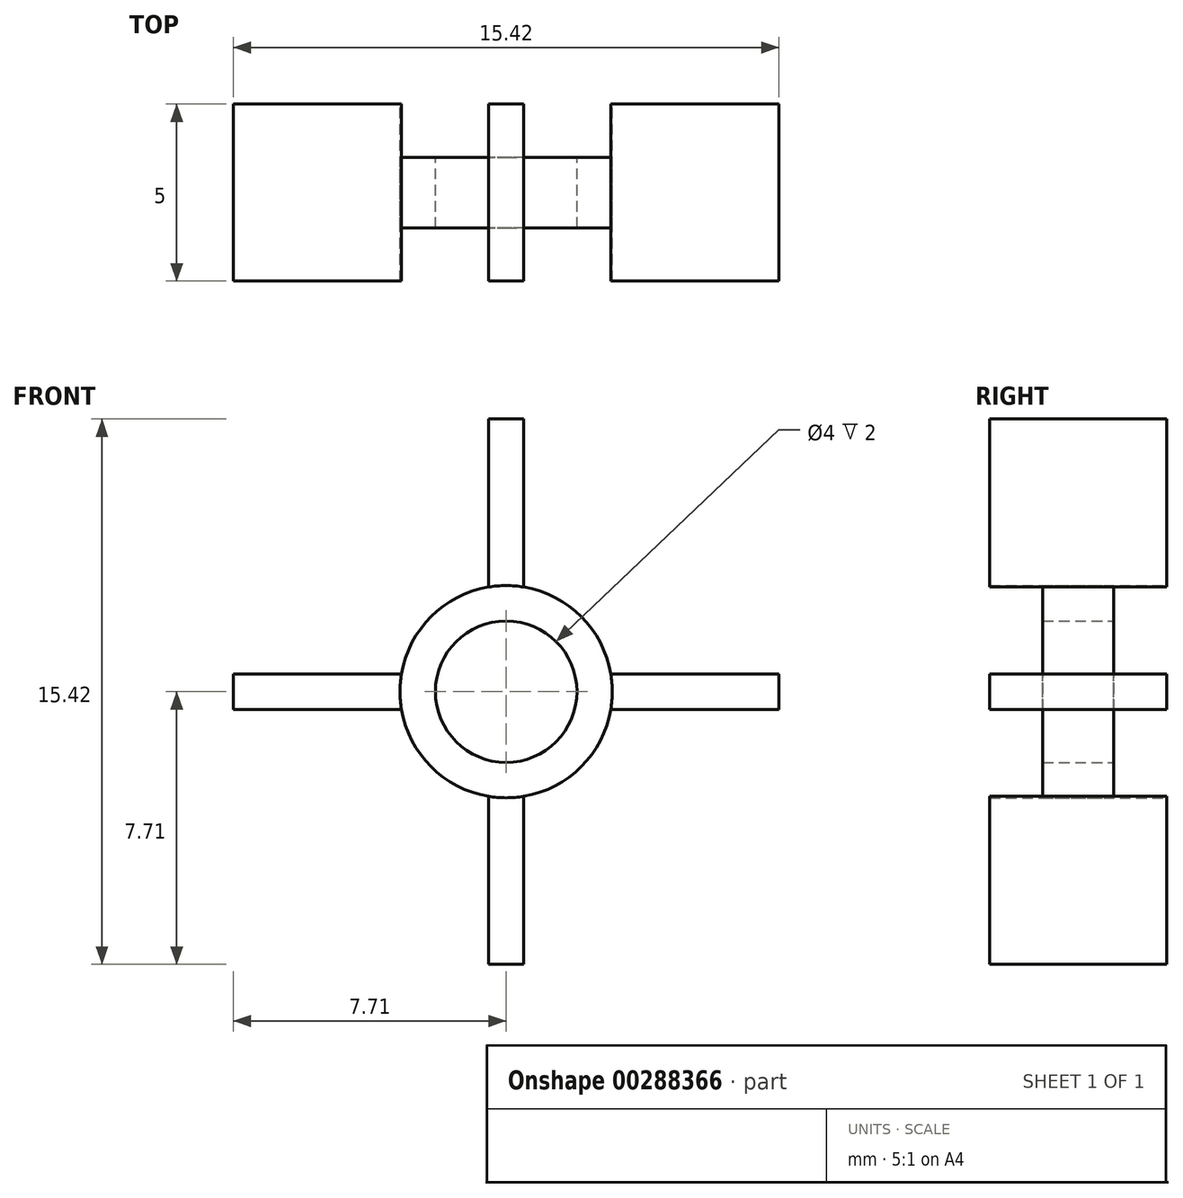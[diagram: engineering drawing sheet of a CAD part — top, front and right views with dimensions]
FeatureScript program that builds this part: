
annotation { "Feature Type Name" : "Feature", "Feature Type Description" : "" }
export const myFeature = defineFeature(function(context is Context, id is Id, definition is map)
    precondition{}
    {
        {
            var Q0;
            Q0=qCreatedBy(makeId("Front.planeOp"),FACE);
            var sketch = newSketch(context, id + "F0", { "sketchPlane" : qUnion([Q0])});
            skCircle(sketch, "E0", {"center": v(0, 0) * mm, "radius": 2 * mm});
            skCircle(sketch, "E1.0", {"center": v(0, 0) * mm, "radius": 3 * mm});
            skLineSegment(sketch, "E2.bottom", {"start": v(2.96, 0.5) * mm, "end": v(7.7, 0.5) * mm});
            skLineSegment(sketch, "E2.top", {"start": v(2.96, -0.5) * mm, "end": v(7.7, -0.5) * mm});
            skLineSegment(sketch, "E2.right", {"start": v(7.7, 0.5) * mm, "end": v(7.7, -0.5) * mm});
            skPoint(sketch, "E2.middle", {"position": v(5.33, 0) * mm});
            skLineSegment(sketch, "E3", {"start": v(0, 3) * mm, "end": v(0, -3) * mm, "construction": true});
            skPoint(sketch, "E4.MirrorP", {"position": v(-5.33, 0) * mm});
            skLineSegment(sketch, "E5.MirrorCS", {"start": v(-7.7, 0.5) * mm, "end": v(-7.7, -0.5) * mm});
            skLineSegment(sketch, "E6.MirrorCS", {"start": v(-2.96, 0.5) * mm, "end": v(-7.7, 0.5) * mm});
            skLineSegment(sketch, "E7.MirrorCS", {"start": v(-2.96, -0.5) * mm, "end": v(-7.7, -0.5) * mm});
            skLineSegment(sketch, "E8.top", {"start": v(0.5, 7.7) * mm, "end": v(-0.5, 7.7) * mm});
            skLineSegment(sketch, "E8.left", {"start": v(0.5, 2.96) * mm, "end": v(0.5, 7.7) * mm});
            skLineSegment(sketch, "E8.right", {"start": v(-0.5, 2.96) * mm, "end": v(-0.5, 7.7) * mm});
            skPoint(sketch, "E8.middle", {"position": v(0, 5.33) * mm});
            skLineSegment(sketch, "E9", {"start": v(-3, 0) * mm, "end": v(3, 0) * mm, "construction": true});
            skLineSegment(sketch, "E10.MirrorCS", {"start": v(0.5, -7.7) * mm, "end": v(-0.5, -7.7) * mm});
            skLineSegment(sketch, "E11.MirrorCS", {"start": v(0.5, -2.96) * mm, "end": v(0.5, -7.7) * mm});
            skLineSegment(sketch, "E12.MirrorCS", {"start": v(-0.5, -2.96) * mm, "end": v(-0.5, -7.7) * mm});
            skSolve(sketch);
        }
        {
            var Q0;
            Q0=makeQuery(id+"F0.imprint","IMPRINT",FACE,{"disambiguationData":[TD([[makeQuery(id+"F0.imprint","IMPRINT",EDGE,{"derivedFrom":sQuery(id+"F0.wireOp",EDGE,"E8.top")}),1.0]])]});
            var Q1;
            Q1=makeQuery(id+"F0.imprint","IMPRINT",FACE,{"disambiguationData":[TD([[makeQuery(id+"F0.imprint","IMPRINT",EDGE,{"derivedFrom":sQuery(id+"F0.wireOp",EDGE,"E5.MirrorCS")}),1.0]])]});
            var Q2;
            Q2=makeQuery(id+"F0.imprint","IMPRINT",FACE,{"disambiguationData":[TD([[makeQuery(id+"F0.imprint","IMPRINT",EDGE,{"derivedFrom":sQuery(id+"F0.wireOp",EDGE,"E10.MirrorCS")}),-1.0]])]});
            var Q3;
            {var subQ0=sQuery(id+"F0.wireOp",EDGE,"E2.bottom");Q3=makeQuery(id+"F0.imprint","IMPRINT",FACE,{"disambiguationData":[TD([[makeQuery(id+"F0.imprint","IMPRINT",EDGE,{"derivedFrom":subQ0}),-1.0]])]});}
            extrude(context, id + "F1", {"entities" : qUnion([Q0, Q1, Q2, Q3]), "endBound" : BoundingType.SYMMETRIC, "depth" : 5 * mm});
        }
        {
            var Q0;
            Q0=makeQuery(id+"F0.imprint","IMPRINT",FACE,{"disambiguationData":[TD([[makeQuery(id+"F0.imprint","IMPRINT",EDGE,{"derivedFrom":sQuery(id+"F0.wireOp",EDGE,"E0")}),-1.0]])]});
            extrude(context, id + "F2", {"entities" : qUnion([Q0]), "endBound" : BoundingType.SYMMETRIC, "depth" : 2 * mm});
        }
    });
